# Revit family: LED Concealed Cove
name_source: partatom
category: Lighting Fixtures
units: mm (PartAtom-declared; Revit-internal decimal feet)

## family parameters
Cut with Voids When Loaded = No
Host = Face
Light Source = Yes
OmniClass Number = 23.80.70.11.14.17
OmniClass Title = Direct/Indirect
Part Type = Normal
Room Calculation Point = No
Round Connector Dimension = Use Diameter
Shared = Yes

## types (5) — shared parameters
Apparent Load = 0 VA
Assembly Code = D5020210
Backbox = Paint - Matte White
Color Filter = 16777215
Default Elevation = 48 "
Description = Concealed LED Cove-15 is designed for installation into a field-constructed architectural cove
Dimming Lamp Color Temperature Shift = <None>
Emit Shape Visible in Rendering = No
Emit from Rectangle Length = 1.5 "
Glass = White Glass
Lamp = LED
Light Distribution = Asymmetric Indirect
Load Classification = Lighting
Manufacturer = Litecontrol
Model = LED Concealed Cove
Mounting = Perimeter
Photometric Web File = 15L-CC-AI-02-Cx-35K-I030.ies
Power Factor = 1
Tilt Angle = 90.00°
Type Comments = Lighting Fixture
URL = https://www.currentlighting.com
Voltage = 120 V
Warranty = 5 years warranty

## per-type parameters (varying)
| type | Emit from Rectangle Width | zz Length 1 |
| 15L-CC-04 | 47.75 " | 48 " |
| 15L-CC-02 | 23.813 " | 24.063 " |
| 15L-CC-03 | 35.781 " | 36.031 " |
| 15L-CC-06 | 71.75 " | 72 " |
| 15L-CC-08 | 95.75 " | 96 " |

## geometry (parser evidence)
native form markers: Sweep x3
no freeform markers — native parametric forms only
